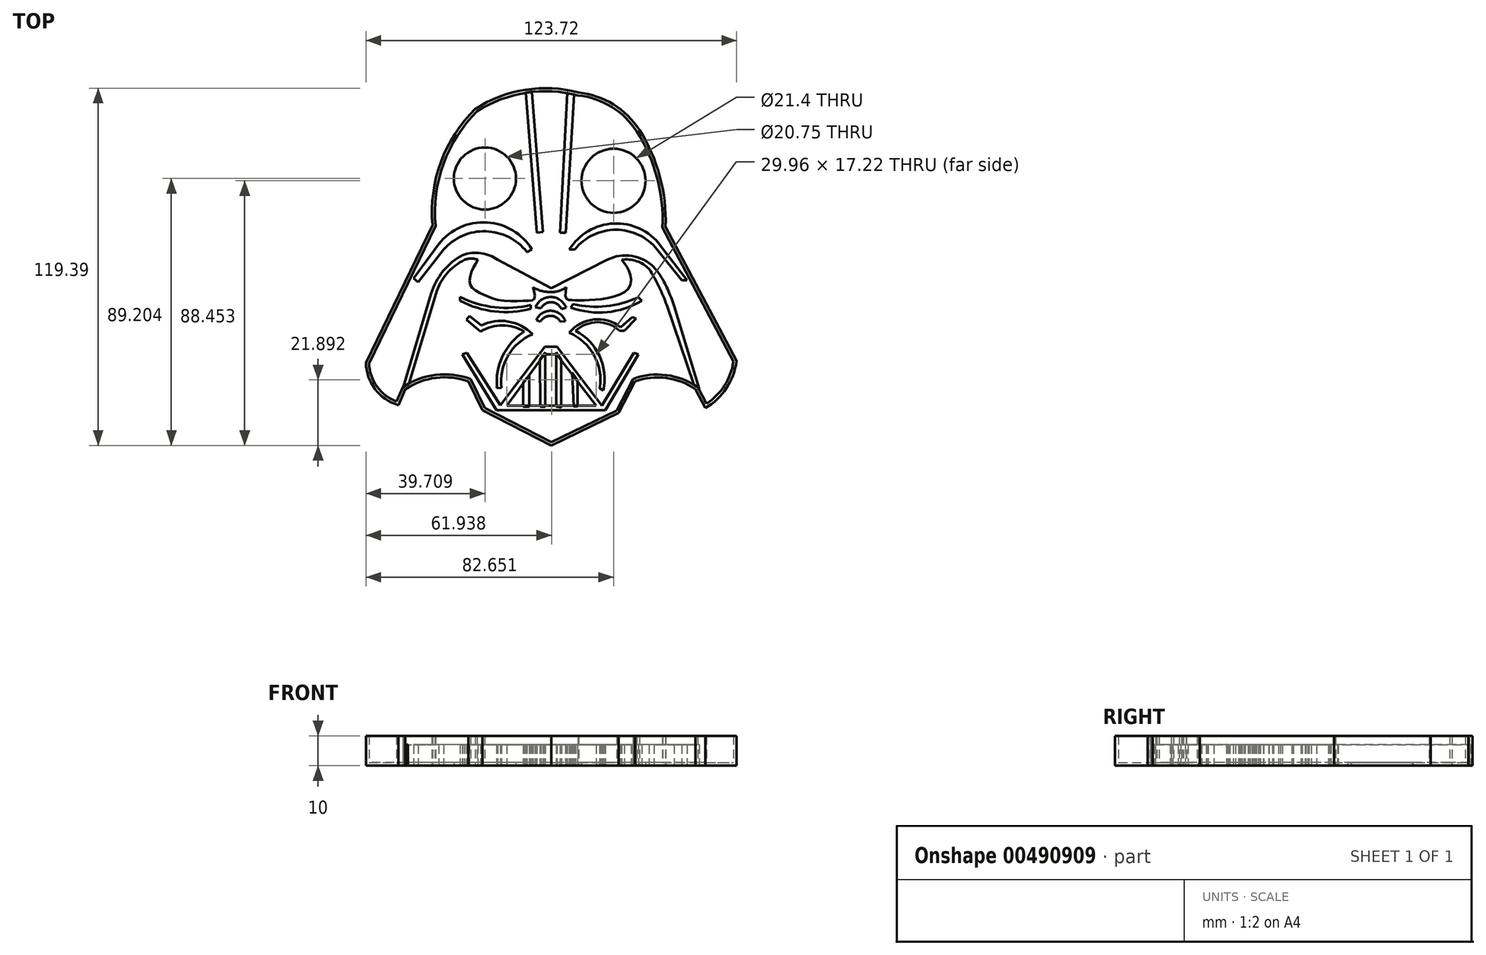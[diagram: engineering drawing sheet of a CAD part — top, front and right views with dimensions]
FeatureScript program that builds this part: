
annotation { "Feature Type Name" : "Feature", "Feature Type Description" : "" }
export const myFeature = defineFeature(function(context is Context, id is Id, definition is map)
    precondition{}
    {
        {
            var Q0;
            Q0=qCreatedBy(makeId("Top.planeOp"),FACE);
            var sketch = newSketch(context, id + "F0", { "sketchPlane" : qUnion([Q0])});
            skArc(sketch, "E0", {"start": v(-25.3, 50.43) * mm, "mid": v(-36.83, 32.6) * mm, "end": v(-39.61, 11.55) * mm});
            skArc(sketch, "E1", {"start": v(9.16, 55.9) * mm, "mid": v(-8.64, 56.78) * mm, "end": v(-25.3, 50.43) * mm});
            skArc(sketch, "E2", {"start": v(29.48, 43.36) * mm, "mid": v(20.74, 51.93) * mm, "end": v(9.16, 55.9) * mm});
            skLineSegment(sketch, "E3", {"start": v(-39.61, 11.55) * mm, "end": v(-61.83, -34.4) * mm});
            skArc(sketch, "E4", {"start": v(38.2, 11.04) * mm, "mid": v(36.28, 27.86) * mm, "end": v(29.48, 43.36) * mm});
            skLineSegment(sketch, "E5", {"start": v(38.2, 11.04) * mm, "end": v(61.9, -33.82) * mm});
            skArc(sketch, "E6", {"start": v(-61.83, -34.4) * mm, "mid": v(-58.77, -43.26) * mm, "end": v(-51.05, -48.57) * mm});
            skLineSegment(sketch, "E7", {"start": v(0, -62.07) * mm, "end": v(-23, -50.21) * mm});
            skLineSegment(sketch, "E8", {"start": v(-23, -50.21) * mm, "end": v(-27.61, -40.66) * mm});
            skLineSegment(sketch, "E9", {"start": v(0, -62.07) * mm, "end": v(22.59, -51.17) * mm});
            skLineSegment(sketch, "E10", {"start": v(22.59, -51.17) * mm, "end": v(28, -40.66) * mm});
            skArc(sketch, "E11", {"start": v(51.46, -49.56) * mm, "mid": v(58.5, -42.9) * mm, "end": v(61.9, -33.82) * mm});
            skLineSegment(sketch, "E12", {"start": v(-51.05, -48.57) * mm, "end": v(-48.7, -43.26) * mm});
            skPoint(sketch, "E12.endSnap0", {"position": v(-58.77, -43.26) * mm});
            skLineSegment(sketch, "E13", {"start": v(51.46, -49.56) * mm, "end": v(48.16, -43.26) * mm});
            skArc(sketch, "E14", {"start": v(-27.61, -40.66) * mm, "mid": v(-38.46, -39.46) * mm, "end": v(-48.7, -43.26) * mm});
            skArc(sketch, "E15", {"start": v(48.16, -43.26) * mm, "mid": v(38.4, -39.54) * mm, "end": v(28, -40.66) * mm});
            skSolve(sketch);
        }
        {
            var Q0;
            Q0=qCreatedBy(makeId("Top.planeOp"),FACE);
            var sketch = newSketch(context, id + "F1", { "sketchPlane" : qUnion([Q0])});
            skLineSegment(sketch, "E16", {"start": v(-18.29, -50.27) * mm, "end": v(-2.1, -29.04) * mm});
            skLineSegment(sketch, "E17", {"start": v(-2.1, -29.04) * mm, "end": v(1.9, -29.04) * mm});
            skLineSegment(sketch, "E18", {"start": v(1.9, -29.04) * mm, "end": v(18.06, -50.27) * mm});
            skLineSegment(sketch, "E19", {"start": v(18.06, -50.27) * mm, "end": v(-18.29, -50.27) * mm});
            skLineSegment(sketch, "E20", {"start": v(-14.87, -48.79) * mm, "end": v(-2.29, -31.57) * mm});
            skLineSegment(sketch, "E21", {"start": v(-2.29, -31.57) * mm, "end": v(1.76, -31.57) * mm});
            skLineSegment(sketch, "E22", {"start": v(1.76, -31.57) * mm, "end": v(15.09, -48.79) * mm});
            skLineSegment(sketch, "E23", {"start": v(15.09, -48.79) * mm, "end": v(-14.87, -48.79) * mm});
            skLineSegment(sketch, "E24", {"start": v(-3.79, -33.62) * mm, "end": v(3.34, -33.62) * mm});
            skLineSegment(sketch, "E25", {"start": v(3.34, -33.62) * mm, "end": v(3.34, -48.79) * mm});
            skLineSegment(sketch, "E26", {"start": v(3.34, -48.79) * mm, "end": v(1.75, -48.79) * mm});
            skLineSegment(sketch, "E27", {"start": v(1.75, -48.79) * mm, "end": v(1.75, -33.62) * mm});
            skLineSegment(sketch, "E28", {"start": v(1.75, -33.62) * mm, "end": v(-2.3, -33.62) * mm});
            skLineSegment(sketch, "E29", {"start": v(-2.3, -33.62) * mm, "end": v(-2.3, -48.79) * mm});
            skLineSegment(sketch, "E30", {"start": v(-3.79, -48.79) * mm, "end": v(-3.79, -33.62) * mm});
            skLineSegment(sketch, "E31", {"start": v(-9.23, -48.79) * mm, "end": v(-9.23, -41.07) * mm});
            skLineSegment(sketch, "E32", {"start": v(-7.5, -48.79) * mm, "end": v(-7.5, -38.7) * mm});
            skLineSegment(sketch, "E33", {"start": v(8.97, -48.79) * mm, "end": v(8.97, -41.07) * mm});
            skLineSegment(sketch, "E34", {"start": v(7.1, -48.79) * mm, "end": v(7.1, -38.7) * mm});
            skLineSegment(sketch, "E35", {"start": v(-6.47, 57.07) * mm, "end": v(-3.11, 9) * mm});
            skLineSegment(sketch, "E36", {"start": v(-3.11, 9) * mm, "end": v(-4.73, 9) * mm});
            skLineSegment(sketch, "E37", {"start": v(-4.73, 9) * mm, "end": v(-8.37, 56.78) * mm});
            skLineSegment(sketch, "E38", {"start": v(2.96, 8.93) * mm, "end": v(4.3, 8.93) * mm});
            skLineSegment(sketch, "E39", {"start": v(4.3, 8.93) * mm, "end": v(7.55, 56.3) * mm});
            skLineSegment(sketch, "E40", {"start": v(2.96, 8.93) * mm, "end": v(6.56, 56.5) * mm});
            skArc(sketch, "E41", {"start": v(-30.4, -13.71) * mm, "mid": v(-18.84, -17.28) * mm, "end": v(-6.79, -16.34) * mm});
            skLineSegment(sketch, "E42", {"start": v(-30.4, -13.71) * mm, "end": v(-30.4, -12.4) * mm});
            skLineSegment(sketch, "E43", {"start": v(-6.79, -16.34) * mm, "end": v(-6.79, -15.12) * mm});
            skArc(sketch, "E44", {"start": v(-30.4, -12.4) * mm, "mid": v(-18.83, -15.9) * mm, "end": v(-6.79, -15.12) * mm});
            skArc(sketch, "E45", {"start": v(5, -15.97) * mm, "mid": v(-0.1, -12.47) * mm, "end": v(-5.28, -15.88) * mm});
            skLineSegment(sketch, "E46", {"start": v(-5.28, -15.88) * mm, "end": v(-3.37, -16.19) * mm});
            skLineSegment(sketch, "E47", {"start": v(5, -15.97) * mm, "end": v(3.42, -16.45) * mm});
            skArc(sketch, "E48", {"start": v(3.42, -16.45) * mm, "mid": v(0.1, -14.21) * mm, "end": v(-3.37, -16.19) * mm});
            skArc(sketch, "E49", {"start": v(4.74, -20.5) * mm, "mid": v(-0.01, -17.06) * mm, "end": v(-4.97, -20.2) * mm});
            skArc(sketch, "E50", {"start": v(3.1, -20.74) * mm, "mid": v(-0.24, -18.73) * mm, "end": v(-3.6, -20.7) * mm});
            skLineSegment(sketch, "E51", {"start": v(-4.97, -20.2) * mm, "end": v(-3.6, -20.7) * mm});
            skLineSegment(sketch, "E52", {"start": v(3.1, -20.74) * mm, "end": v(4.74, -20.5) * mm});
            skArc(sketch, "E53", {"start": v(-6.23, -24.9) * mm, "mid": v(-14.44, -32.12) * mm, "end": v(-16.55, -42.85) * mm});
            skArc(sketch, "E54", {"start": v(-9.02, -23.97) * mm, "mid": v(-16.2, -32.17) * mm, "end": v(-18.09, -42.9) * mm});
            skArc(sketch, "E55", {"start": v(-9.02, -23.97) * mm, "mid": v(-16.29, -21.9) * mm, "end": v(-23.55, -23.97) * mm});
            skArc(sketch, "E56", {"start": v(-6.23, -24.9) * mm, "mid": v(-14.3, -20.65) * mm, "end": v(-23.32, -21.9) * mm});
            skPoint(sketch, "E56.endSnap0", {"position": v(-16.29, -21.9) * mm});
            skLineSegment(sketch, "E57", {"start": v(-23.55, -23.97) * mm, "end": v(-28.31, -20.01) * mm});
            skLineSegment(sketch, "E58", {"start": v(-28.31, -20.01) * mm, "end": v(-27.27, -18.76) * mm});
            skLineSegment(sketch, "E59", {"start": v(-27.27, -18.76) * mm, "end": v(-23.32, -21.9) * mm});
            skLineSegment(sketch, "E60", {"start": v(-18.09, -42.9) * mm, "end": v(-16.55, -42.85) * mm});
            skLineSegment(sketch, "E61", {"start": v(16.23, -42.9) * mm, "end": v(17.47, -43.68) * mm});
            skArc(sketch, "E62", {"start": v(16.23, -42.9) * mm, "mid": v(14.3, -31.9) * mm, "end": v(6.03, -24.4) * mm});
            skArc(sketch, "E63", {"start": v(17.47, -43.68) * mm, "mid": v(16.12, -32.17) * mm, "end": v(8.18, -23.71) * mm});
            skArc(sketch, "E64", {"start": v(23.16, -22.58) * mm, "mid": v(14.22, -19.97) * mm, "end": v(6.03, -24.4) * mm});
            skArc(sketch, "E65", {"start": v(22.86, -23.71) * mm, "mid": v(15.52, -20.88) * mm, "end": v(8.18, -23.71) * mm});
            skLineSegment(sketch, "E66", {"start": v(23.16, -22.58) * mm, "end": v(27.06, -19.1) * mm});
            skLineSegment(sketch, "E67", {"start": v(27.06, -19.1) * mm, "end": v(28.35, -19.67) * mm});
            skLineSegment(sketch, "E68", {"start": v(28.35, -19.67) * mm, "end": v(24.42, -23.71) * mm});
            skLineSegment(sketch, "E69", {"start": v(24.42, -23.71) * mm, "end": v(22.86, -23.71) * mm});
            skArc(sketch, "E70", {"start": v(6.56, -15.97) * mm, "mid": v(18.66, -17.52) * mm, "end": v(30.22, -13.65) * mm});
            skArc(sketch, "E71", {"start": v(7.31, -14.88) * mm, "mid": v(18.4, -15.5) * mm, "end": v(29.1, -12.52) * mm});
            skLineSegment(sketch, "E72", {"start": v(7.31, -14.88) * mm, "end": v(6.56, -15.97) * mm});
            skLineSegment(sketch, "E73", {"start": v(29.1, -12.52) * mm, "end": v(30.22, -13.65) * mm});
            skLineSegment(sketch, "E74", {"start": v(-29.74, -31.57) * mm, "end": v(-18.29, -50.27) * mm});
            skLineSegment(sketch, "E75", {"start": v(-29.74, -31.57) * mm, "end": v(-28.13, -31.05) * mm});
            skLineSegment(sketch, "E76", {"start": v(-28.13, -31.05) * mm, "end": v(-16.91, -48.79) * mm});
            skLineSegment(sketch, "E77", {"start": v(18.06, -50.27) * mm, "end": v(29.1, -31.57) * mm});
            skLineSegment(sketch, "E78", {"start": v(29.1, -31.57) * mm, "end": v(27.54, -31.15) * mm});
            skLineSegment(sketch, "E79", {"start": v(27.54, -31.15) * mm, "end": v(16.93, -48.79) * mm});
            skArc(sketch, "E80", {"start": v(-8.12, 2.6) * mm, "mid": v(-21.81, 9.51) * mm, "end": v(-35.88, 3.43) * mm});
            skArc(sketch, "E81", {"start": v(-6.38, 3.43) * mm, "mid": v(-21.48, 12.47) * mm, "end": v(-37.52, 5.23) * mm});
            skLineSegment(sketch, "E82", {"start": v(-8.12, 2.6) * mm, "end": v(-6.38, 3.43) * mm});
            skLineSegment(sketch, "E83", {"start": v(-35.88, 3.43) * mm, "end": v(-44.36, -7.44) * mm});
            skLineSegment(sketch, "E84", {"start": v(-44.36, -7.44) * mm, "end": v(-45.95, -6.2) * mm});
            skLineSegment(sketch, "E85", {"start": v(-45.95, -6.2) * mm, "end": v(-37.52, 5.23) * mm});
            skArc(sketch, "E86", {"start": v(36.39, 4.86) * mm, "mid": v(20.85, 12.11) * mm, "end": v(6.06, 3.43) * mm});
            skLineSegment(sketch, "E87", {"start": v(35.4, 3.43) * mm, "end": v(43.65, -6.82) * mm});
            skLineSegment(sketch, "E88", {"start": v(43.65, -6.82) * mm, "end": v(45.36, -6.82) * mm});
            skLineSegment(sketch, "E89", {"start": v(45.36, -6.82) * mm, "end": v(36.39, 4.86) * mm});
            skArc(sketch, "E90", {"start": v(35.4, 3.43) * mm, "mid": v(21.64, 10) * mm, "end": v(7.88, 3.43) * mm});
            skLineSegment(sketch, "E91", {"start": v(6.06, 3.43) * mm, "end": v(7.88, 3.43) * mm});
            skFitSpline(sketch, "E92", {"points": [v(-24.52, 0) * mm, v(-26.81, -4.66) * mm, v(-26.81, -8.8) * mm, v(-23.22, -11.32) * mm, v(-17.4, -13.46) * mm, v(-7.98, -13.69) * mm, v(-5.6, -13) * mm, v(-6.07, -9.17) * mm], "startDerivative": vector(-18.16, -30.82) * mm, "endDerivative": vector(-9.98, 36.77) * mm});
            skLineSegment(sketch, "E93", {"start": v(-47.53, -41.66) * mm, "end": v(-38.5, -11.32) * mm});
            skLineSegment(sketch, "E94", {"start": v(-47.53, -41.66) * mm, "end": v(-47.87, -42.78) * mm});
            skLineSegment(sketch, "E95", {"start": v(-47.87, -42.78) * mm, "end": v(-48.73, -43.23) * mm});
            skLineSegment(sketch, "E96", {"start": v(-48.73, -43.23) * mm, "end": v(-49.51, -43) * mm});
            skLineSegment(sketch, "E97", {"start": v(-49.51, -43) * mm, "end": v(-40.08, -11.32) * mm});
            skArc(sketch, "E98", {"start": v(-29.54, 1.6) * mm, "mid": v(-36.1, -3.81) * mm, "end": v(-40.08, -11.32) * mm});
            skArc(sketch, "E99", {"start": v(-28.87, 0) * mm, "mid": v(-34.87, -4.65) * mm, "end": v(-38.5, -11.32) * mm});
            skArc(sketch, "E100", {"start": v(-24.52, 0) * mm, "mid": v(-26.7, 0.38) * mm, "end": v(-28.87, 0) * mm});
            skArc(sketch, "E101", {"start": v(-17.8, 0) * mm, "mid": v(-23.49, 2.17) * mm, "end": v(-29.54, 1.6) * mm});
            skLineSegment(sketch, "E102", {"start": v(-17.8, 0) * mm, "end": v(0, -9.47) * mm});
            skLineSegment(sketch, "E103", {"start": v(0, -9.47) * mm, "end": v(18.73, 0) * mm});
            skArc(sketch, "E104", {"start": v(-6.07, -9.17) * mm, "mid": v(-3.16, -10.45) * mm, "end": v(0, -10.72) * mm});
            skArc(sketch, "E105", {"start": v(0, -10.72) * mm, "mid": v(2.66, -10.41) * mm, "end": v(5.03, -9.17) * mm});
            skFitSpline(sketch, "E106", {"points": [v(5.03, -9.17) * mm, v(5.03, -12.95) * mm, v(6.73, -13.46) * mm, v(10.9, -13.55) * mm, v(19.32, -12.7) * mm, v(26.13, -9.17) * mm, v(26.13, -4.02) * mm, v(23.57, 0) * mm], "startDerivative": vector(-5.52, -37.2) * mm, "endDerivative": vector(-20.55, 25.98) * mm});
            skArc(sketch, "E107", {"start": v(34.33, -2.5) * mm, "mid": v(26.94, 1.28) * mm, "end": v(18.73, 0) * mm});
            skArc(sketch, "E108", {"start": v(32.7, -3.06) * mm, "mid": v(28.5, -0.45) * mm, "end": v(23.57, 0) * mm});
            skArc(sketch, "E109", {"start": v(38.6, -15.2) * mm, "mid": v(36, -8.96) * mm, "end": v(32.7, -3.06) * mm});
            skFitSpline(sketch, "E110", {"points": [v(34.33, -2.5) * mm, v(37.29, -6.67) * mm, v(41.12, -15.42) * mm], "startDerivative": vector(7.08, -8.73) * mm, "endDerivative": vector(6.52, -16.68) * mm});
            skLineSegment(sketch, "E111", {"start": v(41.12, -15.42) * mm, "end": v(49.45, -43.11) * mm});
            skLineSegment(sketch, "E112", {"start": v(49.45, -43.11) * mm, "end": v(48.28, -43.47) * mm});
            skLineSegment(sketch, "E113", {"start": v(48.28, -43.47) * mm, "end": v(38.6, -15.2) * mm});
            skSolve(sketch);
        }
        {
            var Q0;
            Q0 = qSketchRegion(id + "F1", true);
            extrude(context, id + "F2", {"entities" : qUnion([Q0]), "depth" : 7 * mm});
        }
        {
            var Q0;
            Q0=makeQuery(id+"F0.imprint","IMPRINT",FACE,{"disambiguationData":[TD([[makeQuery(id+"F0.imprint","IMPRINT",EDGE,{"derivedFrom":sQuery(id+"F0.wireOp",EDGE,"E0")}),1.0]])]});
            extrude(context, id + "F3", {"entities" : qUnion([Q0]), "depth" : 10 * mm});
        }
        {
            var Q0;
            Q0=makeQuery(id+"F3.opExtrude","CAP_FACE",FACE,{"disambiguationData":[OSD([sQuery(id+"F0.wireOp",EDGE,"E0"),sQuery(id+"F0.wireOp",EDGE,"E1"),sQuery(id+"F0.wireOp",EDGE,"E2"),sQuery(id+"F0.wireOp",EDGE,"E3"),sQuery(id+"F0.wireOp",EDGE,"E4"),sQuery(id+"F0.wireOp",EDGE,"E5"),sQuery(id+"F0.wireOp",EDGE,"E6"),sQuery(id+"F0.wireOp",EDGE,"E7"),sQuery(id+"F0.wireOp",EDGE,"E8"),sQuery(id+"F0.wireOp",EDGE,"E9"),sQuery(id+"F0.wireOp",EDGE,"E10"),sQuery(id+"F0.wireOp",EDGE,"E11"),sQuery(id+"F0.wireOp",EDGE,"E12"),sQuery(id+"F0.wireOp",EDGE,"E13"),sQuery(id+"F0.wireOp",EDGE,"E14"),sQuery(id+"F0.wireOp",EDGE,"E15")])],"isStart":false});
            shell(context, id + "F4", {"entities" : qUnion([Q0]), "thickness" : 1 * mm});
        }
        {
            var Q0;
            Q0=qCreatedBy(makeId("Top.planeOp"),FACE);
            var sketch = newSketch(context, id + "F5", { "sketchPlane" : qUnion([Q0])});
            skLineSegment(sketch, "E114", {"start": v(-8.47, 56.21) * mm, "end": v(-4.84, 9.09) * mm});
            skLineSegment(sketch, "E115", {"start": v(-4.84, 9.09) * mm, "end": v(-2.8, 9.24) * mm});
            skLineSegment(sketch, "E116", {"start": v(-2.8, 9.24) * mm, "end": v(-6.45, 56.65) * mm});
            skLineSegment(sketch, "E117", {"start": v(-6.45, 56.65) * mm, "end": v(-8.47, 56.21) * mm});
            skLineSegment(sketch, "E118", {"start": v(3, 9.09) * mm, "end": v(4.82, 9.09) * mm});
            skLineSegment(sketch, "E119", {"start": v(4.82, 9.09) * mm, "end": v(7.76, 56.21) * mm});
            skLineSegment(sketch, "E120", {"start": v(7.76, 56.21) * mm, "end": v(5.36, 56.36) * mm});
            skLineSegment(sketch, "E121", {"start": v(5.36, 56.36) * mm, "end": v(3, 9.09) * mm});
            skLineSegment(sketch, "E122", {"start": v(-7.3, -38.64) * mm, "end": v(-7.3, -49.08) * mm});
            skLineSegment(sketch, "E123", {"start": v(-7.3, -49.08) * mm, "end": v(-9.39, -49.08) * mm});
            skLineSegment(sketch, "E124", {"start": v(-9.39, -49.08) * mm, "end": v(-9.39, -40.98) * mm});
            skLineSegment(sketch, "E125", {"start": v(-9.39, -40.98) * mm, "end": v(-7.3, -38.64) * mm});
            skLineSegment(sketch, "E126", {"start": v(-3.6, -49.1) * mm, "end": v(-2, -49.19) * mm});
            skLineSegment(sketch, "E127", {"start": v(-2, -49.19) * mm, "end": v(-2, -30.95) * mm});
            skLineSegment(sketch, "E128", {"start": v(-2, -30.95) * mm, "end": v(-3.72, -33.3) * mm});
            skLineSegment(sketch, "E129", {"start": v(-3.72, -33.3) * mm, "end": v(-3.6, -49.1) * mm});
            skLineSegment(sketch, "E130", {"start": v(1.66, -49.1) * mm, "end": v(1.66, -31.01) * mm});
            skLineSegment(sketch, "E131", {"start": v(1.66, -31.01) * mm, "end": v(3.32, -33.13) * mm});
            skLineSegment(sketch, "E132", {"start": v(3.32, -33.13) * mm, "end": v(3.32, -49.34) * mm});
            skLineSegment(sketch, "E133", {"start": v(3.32, -49.34) * mm, "end": v(1.66, -49.1) * mm});
            skLineSegment(sketch, "E134", {"start": v(7, -37.74) * mm, "end": v(7.52, -49.1) * mm});
            skLineSegment(sketch, "E135", {"start": v(7.52, -49.1) * mm, "end": v(8.84, -49.05) * mm});
            skLineSegment(sketch, "E136", {"start": v(8.84, -49.05) * mm, "end": v(8.84, -40.2) * mm});
            skLineSegment(sketch, "E137", {"start": v(8.84, -40.2) * mm, "end": v(7, -37.74) * mm});
            skSolve(sketch);
        }
        {
            var Q0;
            Q0 = qSketchRegion(id + "F5", true);
            extrude(context, id + "F6", {"entities" : qUnion([Q0]), "depth" : 7 * mm});
        }
        {
            var Q0;
            Q0=qCreatedBy(makeId("Top.planeOp"),FACE);
            var sketch = newSketch(context, id + "F7", { "sketchPlane" : qUnion([Q0])});
            skCircle(sketch, "E138", {"center": v(-22.12, 27.13) * mm, "radius": 10.37 * mm});
            skCircle(sketch, "E139", {"center": v(20.82, 26.38) * mm, "radius": 10.7 * mm});
            skSolve(sketch);
        }
        {
            var Q0;
            Q0 = qSketchRegion(id + "F7", true);
            extrude(context, id + "F8", {"entities" : qUnion([Q0]), "operationType" : NewBodyOperationType.REMOVE, "depth" : 2 * mm});
        }
    });
